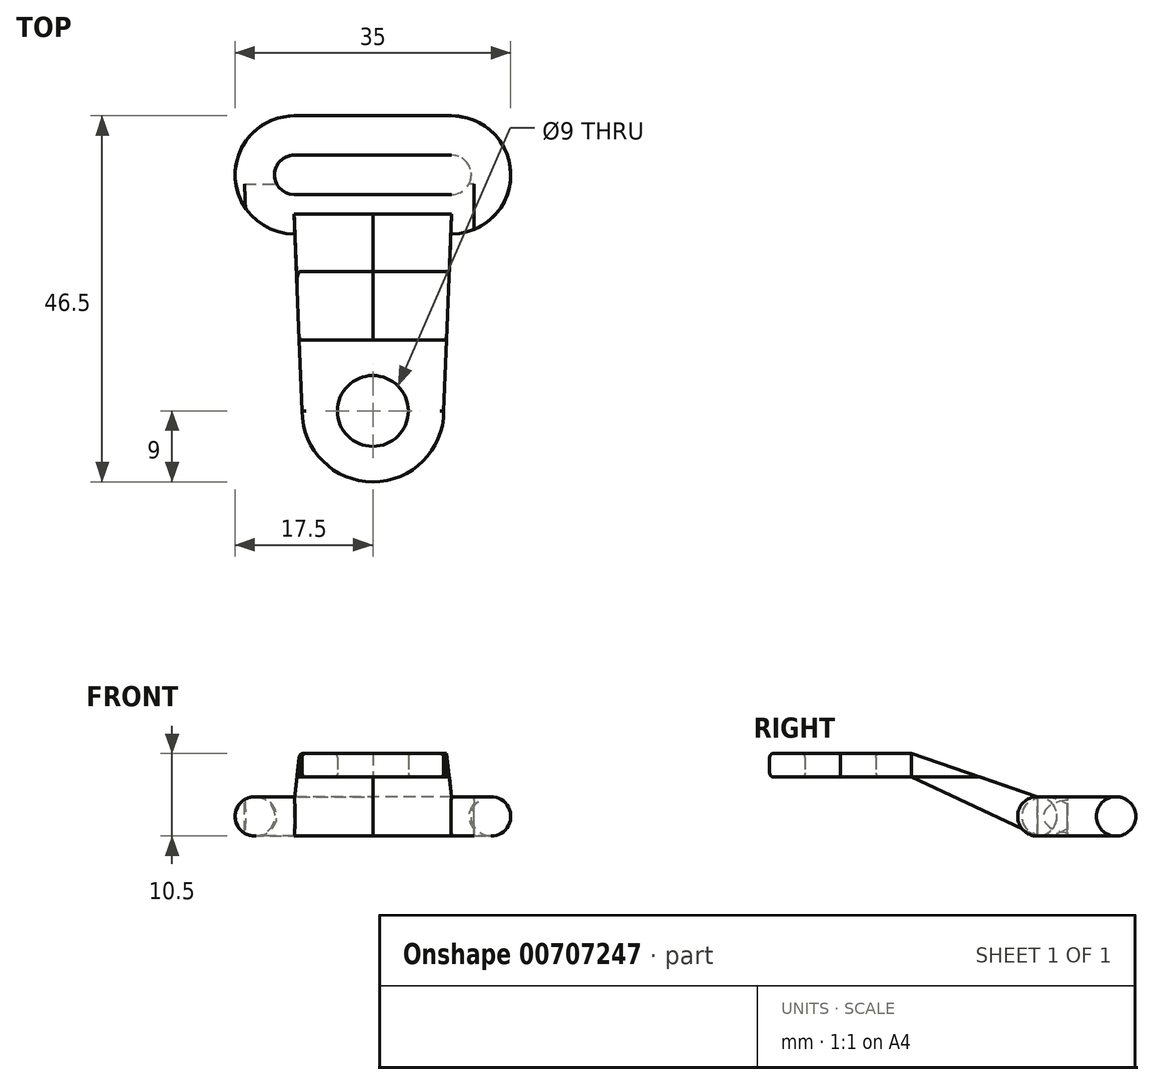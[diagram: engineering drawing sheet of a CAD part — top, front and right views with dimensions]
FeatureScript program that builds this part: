
annotation { "Feature Type Name" : "Feature", "Feature Type Description" : "" }
export const myFeature = defineFeature(function(context is Context, id is Id, definition is map)
    precondition{}
    {
        {
            var Q0;
            Q0=qCreatedBy(makeId("Top.planeOp"),FACE);
            var sketch = newSketch(context, id + "F0", { "sketchPlane" : qUnion([Q0])});
            skLineSegment(sketch, "E0.bottom", {"start": v(-10, 2.5) * mm, "end": v(10, 2.5) * mm});
            skLineSegment(sketch, "E0.top", {"start": v(-10, -2.5) * mm, "end": v(10, -2.5) * mm});
            skPoint(sketch, "E0.middle", {"position": v(0, 0) * mm});
            skLineSegment(sketch, "E1", {"start": v(-10, -7.5) * mm, "end": v(10, -7.5) * mm});
            skLineSegment(sketch, "E2", {"start": v(-10, 7.5) * mm, "end": v(10, 7.5) * mm});
            skArc(sketch, "E3", {"start": v(-10, 7.5) * mm, "mid": v(-17.5, 0) * mm, "end": v(-10, -7.5) * mm});
            skArc(sketch, "E4", {"start": v(10, 7.5) * mm, "mid": v(17.5, 0) * mm, "end": v(10, -7.5) * mm});
            skArc(sketch, "E5", {"start": v(10, -2.5) * mm, "mid": v(12.5, 0) * mm, "end": v(10, 2.5) * mm});
            skArc(sketch, "E6", {"start": v(-10, -2.5) * mm, "mid": v(-12.5, 0) * mm, "end": v(-10, 2.5) * mm});
            skSolve(sketch);
        }
        {
            var Q0;
            Q0=qCreatedBy(makeId("Right.planeOp"),FACE);
            var sketch = newSketch(context, id + "F1", { "sketchPlane" : qUnion([Q0])});
            skPoint(sketch, "E7", {"position": v(-5, 0) * mm});
            skCircle(sketch, "E8", {"center": v(-5, 0) * mm, "radius": 2.5 * mm});
            skPoint(sketch, "E9", {"position": v(5, 0) * mm});
            skCircle(sketch, "E10", {"center": v(5, 0) * mm, "radius": 2.5 * mm});
            skSolve(sketch);
        }
        {
            var Q0;
            Q0=qCreatedBy(makeId("Top.planeOp"),FACE);
            cPlane(context, id + "F2", {"entities" : qUnion([Q0]), "cplaneType" : CPlaneType.OFFSET, "offset" : 5 * mm, "width" : 150 * mm, "height" : 150 * mm});
        }
        {
            var Q0;
            Q0=qCreatedBy(id+"F2.planeOp",FACE);
            var sketch = newSketch(context, id + "F3", { "sketchPlane" : qUnion([Q0])});
            skPoint(sketch, "E11", {"position": v(0, -30) * mm});
            skCircle(sketch, "E12", {"center": v(0, -30) * mm, "radius": 4.5 * mm});
            skCircle(sketch, "E13", {"center": v(0, -30) * mm, "radius": 9 * mm});
            skSolve(sketch);
        }
        {
            var Q0;
            Q0=qSketchRegion(id+"F3",true);
            extrude(context, id + "F4", {"entities" : qUnion([Q0]), "depth" : 3 * mm, "offsetDistance" : 25 * mm});
        }
        {
            var Q0;
            Q0=qCreatedBy(id+"F2.planeOp",FACE);
            var sketch = newSketch(context, id + "F5", { "sketchPlane" : qUnion([Q0])});
            skPoint(sketch, "E14", {"position": v(-37.08, -21.1) * mm});
            skPoint(sketch, "E15", {"position": v(-25.48, -25.42) * mm});
            skPoint(sketch, "E16", {"position": v(0, -30) * mm});
            skPoint(sketch, "E17", {"position": v(17.5, 0) * mm});
            skPoint(sketch, "E18", {"position": v(-17.5, 0) * mm});
            skPoint(sketch, "E19", {"position": v(0, -5) * mm});
            skPoint(sketch, "E20", {"position": v(-10, -5) * mm});
            skPoint(sketch, "E21", {"position": v(10, -5) * mm});
            skLineSegment(sketch, "E22", {"start": v(-10, -5) * mm, "end": v(10, -5) * mm});
            skPoint(sketch, "E23", {"position": v(-9, -30) * mm});
            skPoint(sketch, "E24", {"position": v(9, -30) * mm});
            skLineSegment(sketch, "E25", {"start": v(-9, -30) * mm, "end": v(-10, -5) * mm});
            skLineSegment(sketch, "E26", {"start": v(10, -5) * mm, "end": v(9, -30) * mm});
            skLineSegment(sketch, "E27", {"start": v(-9, -30) * mm, "end": v(-1.42, -23.65) * mm});
            skLineSegment(sketch, "E28", {"start": v(-1.42, -23.65) * mm, "end": v(9, -30) * mm});
            skSolve(sketch);
        }
        {
            var Q0;
            Q0=qSketchRegion(id+"F5",true);
            extrude(context, id + "F6", {"entities" : qUnion([Q0]), "operationType" : NewBodyOperationType.ADD, "depth" : 3 * mm, "offsetDistance" : 25 * mm});
        }
        {
            var Q0;
            Q0=qCreatedBy(id+"F2.planeOp",FACE);
            var sketch = newSketch(context, id + "F7", { "sketchPlane" : qUnion([Q0])});
            skPoint(sketch, "E29", {"position": v(0, -30) * mm});
            skPoint(sketch, "E30", {"position": v(-17.34, -24.35) * mm});
            skPoint(sketch, "E31", {"position": v(0, -21) * mm});
            skLineSegment(sketch, "E32", {"start": v(0, -21) * mm, "end": v(-13.31, -21) * mm});
            skLineSegment(sketch, "E33", {"start": v(-13.31, -21) * mm, "end": v(13.6, -21) * mm});
            skLineSegment(sketch, "E34", {"start": v(13.6, -21) * mm, "end": v(13.6, -1.76) * mm});
            skLineSegment(sketch, "E35", {"start": v(13.6, -1.76) * mm, "end": v(-14.46, -1.76) * mm});
            skLineSegment(sketch, "E36", {"start": v(-14.46, -1.76) * mm, "end": v(-13.31, -21) * mm});
            skSolve(sketch);
        }
        {
            var Q0;
            Q0=qSketchRegion(id+"F7",true);
            extrude(context, id + "F8", {"entities" : qUnion([Q0]), "operationType" : NewBodyOperationType.REMOVE, "depth" : 3.1 * mm, "offsetDistance" : 25 * mm});
        }
        {
            var Q0;
            Q0=qCreatedBy(makeId("Right.planeOp"),FACE);
            var sketch = newSketch(context, id + "F9", { "sketchPlane" : qUnion([Q0])});
            skPoint(sketch, "E37", {"position": v(-5, 0) * mm});
            skPoint(sketch, "E38", {"position": v(-5, 2.5) * mm});
            skPoint(sketch, "E39", {"position": v(-5, -2.5) * mm});
            skPoint(sketch, "E40", {"position": v(-21, 5) * mm});
            skPoint(sketch, "E41", {"position": v(-21, 8) * mm});
            skLineSegment(sketch, "E42", {"start": v(-5, -2.5) * mm, "end": v(-21, 5) * mm});
            skLineSegment(sketch, "E43", {"start": v(-21, 8) * mm, "end": v(-5, 2.5) * mm});
            skLineSegment(sketch, "E44", {"start": v(-21, 8) * mm, "end": v(-21, 5) * mm});
            skLineSegment(sketch, "E45", {"start": v(-5, 2.5) * mm, "end": v(-5, -2.5) * mm});
            skSolve(sketch);
        }
        {
            var Q0;
            Q0=qSketchRegion(id+"F9",true);
            extrude(context, id + "F10", {"entities" : qUnion([Q0]), "depth" : 10 * mm, "offsetDistance" : 25 * mm});
        }
        {
            var Q0;
            Q0=qSketchRegion(id+"F9",true);
            extrude(context, id + "F11", {"entities" : qUnion([Q0]), "oppositeDirection" : true, "depth" : 10 * mm, "offsetDistance" : 25 * mm});
        }
        {
            var Q0;
            Q0=qCreatedBy(id+"F2.planeOp",FACE);
            var sketch = newSketch(context, id + "F12", { "sketchPlane" : qUnion([Q0])});
            skPoint(sketch, "E46", {"position": v(10, -5) * mm});
            skPoint(sketch, "E47", {"position": v(9.36, -21) * mm});
            skPoint(sketch, "E48", {"position": v(-9.36, -21) * mm});
            skPoint(sketch, "E49", {"position": v(-10, -5) * mm});
            skLineSegment(sketch, "E50", {"start": v(-10, -5) * mm, "end": v(-9.36, -21) * mm});
            skLineSegment(sketch, "E51", {"start": v(10, -5) * mm, "end": v(9.36, -21) * mm});
            skLineSegment(sketch, "E52", {"start": v(12.87, -21) * mm, "end": v(12.87, -1.18) * mm});
            skLineSegment(sketch, "E53", {"start": v(12.87, -1.18) * mm, "end": v(-16.31, -1.18) * mm});
            skLineSegment(sketch, "E54", {"start": v(-16.31, -1.18) * mm, "end": v(-15.52, -21) * mm});
            skLineSegment(sketch, "E55", {"start": v(-15.52, -21) * mm, "end": v(-9.36, -21) * mm});
            skLineSegment(sketch, "E56", {"start": v(-10, -5) * mm, "end": v(10, -5) * mm});
            skLineSegment(sketch, "E57", {"start": v(12.87, -21) * mm, "end": v(9.36, -21) * mm});
            skSolve(sketch);
        }
        {
            var Q0;
            Q0 = qSketchRegion(id + "F12", true);
            extrude(context, id + "F13", {"entities" : qUnion([Q0]), "operationType" : NewBodyOperationType.REMOVE, "oppositeDirection" : true, "depth" : 25 * mm, "offsetDistance" : 25 * mm});
        }
        {
            var Q0;
            Q0 = qSketchRegion(id + "F12", true);
            extrude(context, id + "F14", {"entities" : qUnion([Q0]), "operationType" : NewBodyOperationType.REMOVE, "depth" : 25 * mm, "offsetDistance" : 25 * mm});
        }
        {
            var Q0;
            Q0=makeQuery(id+"F1.imprint","IMPRINT",FACE,{"disambiguationData":[TD([[makeQuery(id+"F1.imprint","IMPRINT",EDGE,{"derivedFrom":sQuery(id+"F1.wireOp",EDGE,"E10")}),1.0]])]});
            var Q1;
            Q1=sQuery(id+"F0.wireOp",EDGE,"E2");
            var Q2;
            Q2=sQuery(id+"F0.wireOp",EDGE,"E3");
            var Q3;
            Q3=sQuery(id+"F0.wireOp",EDGE,"E1");
            var Q4;
            Q4=sQuery(id+"F0.wireOp",EDGE,"E4");
            sweep(context, id + "F15", {"profiles" : qUnion([Q0]), "path" : qUnion([Q1, Q2, Q3, Q4])});
        }
        {
            var Q0;
            Q0=makeQuery(id+"F6.opExtrude","CAP_EDGE",EDGE,{"disambiguationData":[OSD([sQuery(id+"F5.wireOp",EDGE,"E25")])],"isStart":false});
            var Q1;
            Q1=makeQuery(id+"F6.opExtrude","CAP_EDGE",EDGE,{"disambiguationData":[OSD([sQuery(id+"F5.wireOp",EDGE,"E25")])],"isStart":true});
            var Q2;
            Q2=makeQuery(id+"F13.boolean.opBoolean","INTERSECT",EDGE,{"derivedFrom":[makeQuery(id+"F11.opExtrude","SWEPT_FACE",FACE,{"disambiguationData":[OSD([sQuery(id+"F9.wireOp",EDGE,"E42")])]}),makeQuery(id+"F13.opExtrude","SWEPT_FACE",FACE,{"disambiguationData":[OSD([sQuery(id+"F12.wireOp",EDGE,"E50")])]})]});
            var Q3;
            Q3=makeQuery(id+"F14.boolean.opBoolean","INTERSECT",EDGE,{"derivedFrom":[makeQuery(id+"F11.opExtrude","SWEPT_FACE",FACE,{"disambiguationData":[OSD([sQuery(id+"F9.wireOp",EDGE,"E43")])]}),makeQuery(id+"F14.opExtrude","SWEPT_FACE",FACE,{"disambiguationData":[OSD([sQuery(id+"F12.wireOp",EDGE,"E50")])]})]});
            var Q4;
            Q4=makeQuery(id+"F4.opExtrude","CAP_EDGE",EDGE,{"disambiguationData":[OSD([sQuery(id+"F3.wireOp",EDGE,"E13")])],"isStart":false});
            var Q5;
            Q5=makeQuery(id+"F4.opExtrude","CAP_EDGE",EDGE,{"disambiguationData":[OSD([sQuery(id+"F3.wireOp",EDGE,"E13")])],"isStart":true});
            var Q6;
            Q6=makeQuery(id+"F4.opExtrude","CAP_EDGE",EDGE,{"disambiguationData":[OSD([sQuery(id+"F3.wireOp",EDGE,"E12")])],"isStart":false});
            var Q7;
            Q7=makeQuery(id+"F4.opExtrude","CAP_EDGE",EDGE,{"disambiguationData":[OSD([sQuery(id+"F3.wireOp",EDGE,"E12")])],"isStart":true});
            var Q8;
            Q8=makeQuery(id+"F13.boolean.opBoolean","INTERSECT",EDGE,{"derivedFrom":[makeQuery(id+"F10.opExtrude","SWEPT_FACE",FACE,{"disambiguationData":[OSD([sQuery(id+"F9.wireOp",EDGE,"E42")])]}),makeQuery(id+"F13.opExtrude","SWEPT_FACE",FACE,{"disambiguationData":[OSD([sQuery(id+"F12.wireOp",EDGE,"E51")])]})]});
            var Q9;
            Q9=makeQuery(id+"F13.boolean.opBoolean","INTERSECT",EDGE,{"derivedFrom":[makeQuery(id+"F10.opExtrude","SWEPT_FACE",FACE,{"disambiguationData":[OSD([sQuery(id+"F9.wireOp",EDGE,"E43")])]}),makeQuery(id+"F13.opExtrude","SWEPT_FACE",FACE,{"disambiguationData":[OSD([sQuery(id+"F12.wireOp",EDGE,"E51")])]})]});
            fillet(context, id + "F16", {"entities" : qUnion([Q0, Q1, Q2, Q3, Q4, Q5, Q6, Q7, Q8, Q9]), "radius" : 0.5 * mm, "tangentPropagation" : true, "allowEdgeOverflow" : false});
        }
    });
